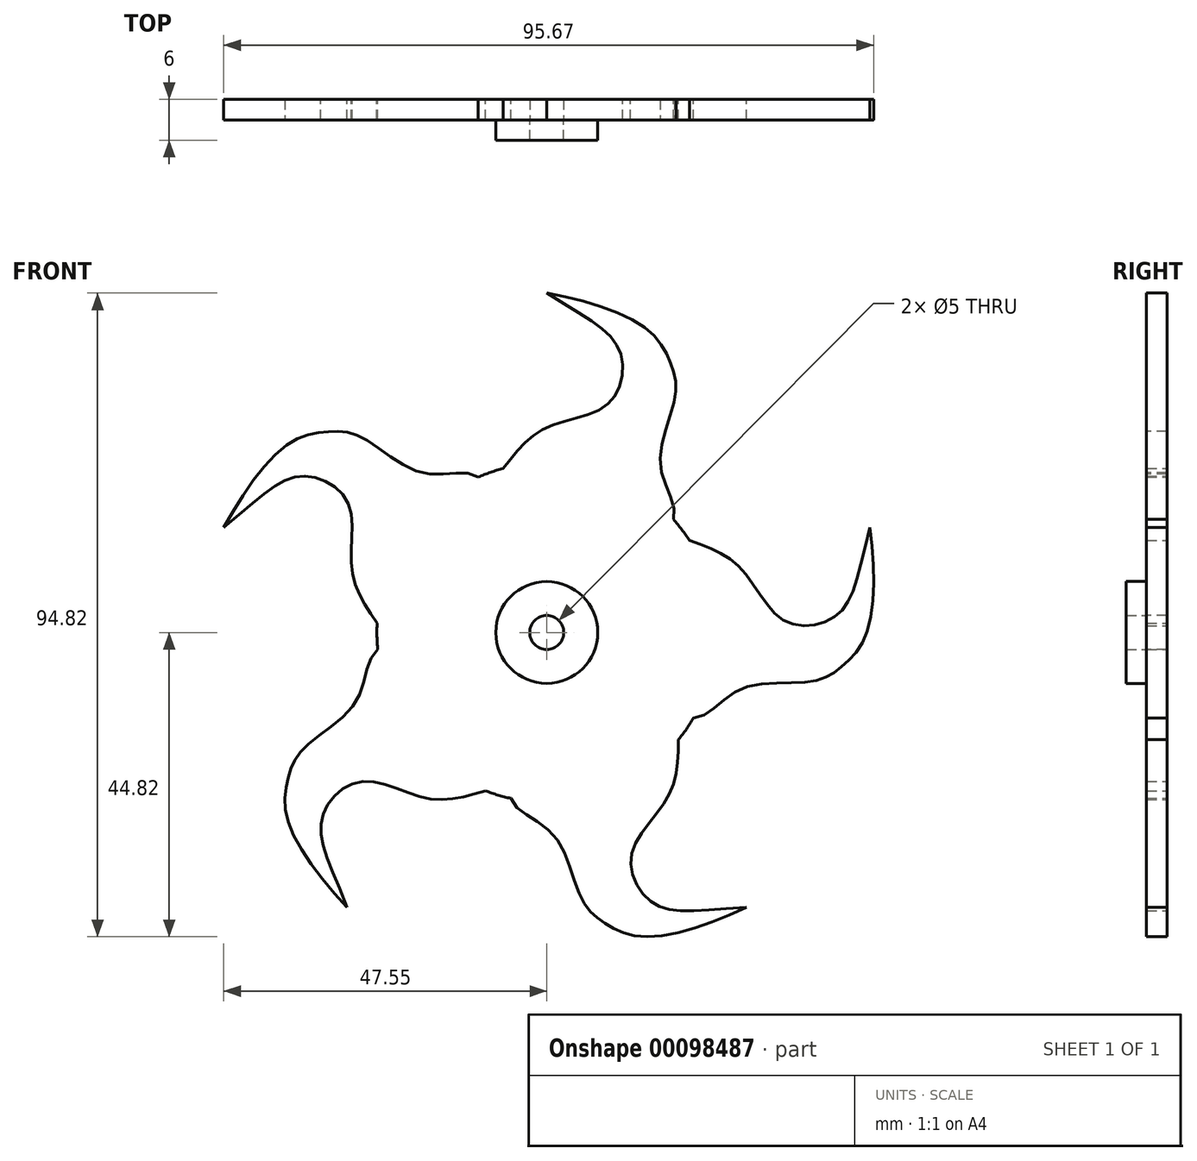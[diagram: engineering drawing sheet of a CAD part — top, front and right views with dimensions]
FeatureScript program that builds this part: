
annotation { "Feature Type Name" : "Feature", "Feature Type Description" : "" }
export const myFeature = defineFeature(function(context is Context, id is Id, definition is map)
    precondition{}
    {
        {
            var Q0;
            Q0=qCreatedBy(makeId("Front.planeOp"),FACE);
            var sketch = newSketch(context, id + "F0", { "sketchPlane" : qUnion([Q0])});
            skCircle(sketch, "E0", {"center": v(0, 0) * mm, "radius": 50 * mm, "construction": true});
            skCircle(sketch, "E1", {"center": v(0, 0) * mm, "radius": 25 * mm});
            skFitSpline(sketch, "E2", {"points": [v(0, 50) * mm, v(14.6, 44.79) * mm, v(18.26, 39.59) * mm, v(18.9, 34.67) * mm, v(16.74, 24.4) * mm, v(18.65, 16.65) * mm], "startDerivative": vector(61.52, -11.38) * mm, "endDerivative": vector(-10.6, -36.77) * mm});
            skFitSpline(sketch, "E3", {"points": [v(0, 50) * mm, v(10.8, 41.27) * mm, v(9.2, 33.82) * mm, v(0, 30.17) * mm, v(-6.4, 24.17) * mm], "startDerivative": vector(61.6, -38.88) * mm, "endDerivative": vector(-24.26, -32.03) * mm});
            skSolve(sketch);
        }
        {
            var Q0;
            Q0=makeQuery(id+"F0.imprint","IMPRINT",FACE,{"disambiguationData":[TD([[makeQuery(id+"F0.imprint","IMPRINT",EDGE,{"derivedFrom":sQuery(id+"F0.wireOp",EDGE,"E2")}),-1.0]])]});
            var Q1;
            {var subQ0=sQuery(id+"F0.wireOp",EDGE,"E1");var subQ1=makeQuery(id+"F0.imprint","INTERSECT",VERTEX,{"derivedFrom":[subQ0,sQuery(id+"F0.wireOp",EDGE,"E2")]});Q1=makeQuery(id+"F0.imprint","IMPRINT",FACE,{"disambiguationData":[TD([[makeQuery(id+"F0.imprint","IMPRINT",EDGE,{"disambiguationData":[TD([[subQ1,-1.0]])],"derivedFrom":subQ0}),1.0]])]});}
            extrude(context, id + "F1", {"entities" : qUnion([Q0, Q1]), "depth" : 3 * mm});
        }
        {
            var Q0;
            Q0=qCreatedBy(makeId("Right.planeOp"),FACE);
            var sketch = newSketch(context, id + "F2", { "sketchPlane" : qUnion([Q0])});
            skLineSegment(sketch, "E4", {"start": v(-18.7, 0) * mm, "end": v(27.7, 0) * mm, "construction": true});
            skSolve(sketch);
        }
        {
            var Q0;
            Q0=makeQuery(id+"F1.opExtrude","SWEPT_BODY",BODY,{"disambiguationData":[OSD([sQuery(id+"F0.wireOp",EDGE,"E2"),sQuery(id+"F0.wireOp",EDGE,"E3"),sQuery(id+"F0.wireOp",EDGE,"JvflZ2Xm-OZbW-fdge-9bIT-jv6nQqX975Xf")])]});
            var Q1;
            Q1=sQuery(id+"F2.wireOp",EDGE,"E4");
            circularPattern(context, id + "F3", {"entities" : qUnion([Q0]), "axis" : qUnion([Q1]), "angle" : 360 * degree, "instanceCount" : 5, "equalSpace" : true});
        }
        {
            var Q0;
            Q0=makeQuery(id+"F3.opPattern","COPY",FACE,{"derivedFrom":makeQuery(id+"F1.opExtrude","CAP_FACE",FACE,{"disambiguationData":[OSD([sQuery(id+"F0.wireOp",EDGE,"E1"),sQuery(id+"F0.wireOp",EDGE,"E2"),sQuery(id+"F0.wireOp",EDGE,"E3")])],"isStart":false}),"instanceName":"3"});
            var sketch = newSketch(context, id + "F4", { "sketchPlane" : qUnion([Q0])});
            skPoint(sketch, "E5.center", {"position": v(0, 0) * mm});
            skCircle(sketch, "E6", {"center": v(0, 0) * mm, "radius": 2.5 * mm});
            skSolve(sketch);
        }
        {
            var Q0;
            Q0=qSketchRegion(id+"F4",true);
            extrude(context, id + "F5", {"entities" : qUnion([Q0]), "operationType" : NewBodyOperationType.REMOVE, "endBound" : BoundingType.UP_TO_NEXT, "oppositeDirection" : true, "depth" : 25 * mm});
        }
        {
            var Q0;
            Q0=makeQuery(id+"F1.opExtrude","SWEPT_BODY",BODY,{"disambiguationData":[OSD([sQuery(id+"F0.wireOp",EDGE,"E1"),sQuery(id+"F0.wireOp",EDGE,"E2"),sQuery(id+"F0.wireOp",EDGE,"E3")])]});
            var Q1;
            Q1=makeQuery(id+"F3.opPattern","COPY",BODY,{"derivedFrom":makeQuery(id+"F1.opExtrude","SWEPT_BODY",BODY,{"disambiguationData":[OSD([sQuery(id+"F0.wireOp",EDGE,"E1"),sQuery(id+"F0.wireOp",EDGE,"E2"),sQuery(id+"F0.wireOp",EDGE,"E3")])]}),"instanceName":"1"});
            var Q2;
            Q2=makeQuery(id+"F3.opPattern","COPY",BODY,{"derivedFrom":makeQuery(id+"F1.opExtrude","SWEPT_BODY",BODY,{"disambiguationData":[OSD([sQuery(id+"F0.wireOp",EDGE,"E1"),sQuery(id+"F0.wireOp",EDGE,"E2"),sQuery(id+"F0.wireOp",EDGE,"E3")])]}),"instanceName":"2"});
            var Q3;
            Q3=makeQuery(id+"F3.opPattern","COPY",BODY,{"derivedFrom":makeQuery(id+"F1.opExtrude","SWEPT_BODY",BODY,{"disambiguationData":[OSD([sQuery(id+"F0.wireOp",EDGE,"E1"),sQuery(id+"F0.wireOp",EDGE,"E2"),sQuery(id+"F0.wireOp",EDGE,"E3")])]}),"instanceName":"3"});
            var Q4;
            Q4=makeQuery(id+"F3.opPattern","COPY",BODY,{"derivedFrom":makeQuery(id+"F1.opExtrude","SWEPT_BODY",BODY,{"disambiguationData":[OSD([sQuery(id+"F0.wireOp",EDGE,"E1"),sQuery(id+"F0.wireOp",EDGE,"E2"),sQuery(id+"F0.wireOp",EDGE,"E3")])]}),"instanceName":"4"});
            booleanBodies(context, id + "F6", {"operationType" : BooleanOperationType.UNION, "tools" : qUnion([Q0, Q1, Q2, Q3, Q4])});
        }
        {
            var Q0;
            {var subQ0=makeQuery(id+"F1.opExtrude","CAP_FACE",FACE,{"disambiguationData":[OSD([sQuery(id+"F0.wireOp",EDGE,"E1"),sQuery(id+"F0.wireOp",EDGE,"E2"),sQuery(id+"F0.wireOp",EDGE,"E3")])],"isStart":false});Q0=makeQuery(id+"F6.opBoolean","MERGE",FACE,{"derivedFrom":[subQ0,makeQuery(id+"F3.opPattern","COPY",FACE,{"derivedFrom":subQ0,"instanceName":"1"}),makeQuery(id+"F3.opPattern","COPY",FACE,{"derivedFrom":subQ0,"instanceName":"2"}),makeQuery(id+"F3.opPattern","COPY",FACE,{"derivedFrom":subQ0,"instanceName":"3"}),makeQuery(id+"F3.opPattern","COPY",FACE,{"derivedFrom":subQ0,"instanceName":"4"})]});}
            var sketch = newSketch(context, id + "F7", { "sketchPlane" : qUnion([Q0])});
            skCircle(sketch, "E7.0", {"center": v(0, 0) * mm, "radius": 2.5 * mm});
            skCircle(sketch, "E8", {"center": v(0, 0) * mm, "radius": 7.5 * mm});
            skSolve(sketch);
        }
        {
            var Q0;
            Q0 = qSketchRegion(id + "F7", true);
            extrude(context, id + "F8", {"entities" : qUnion([Q0]), "depth" : 3 * mm, "offsetDistance" : 25 * mm});
        }
    });
